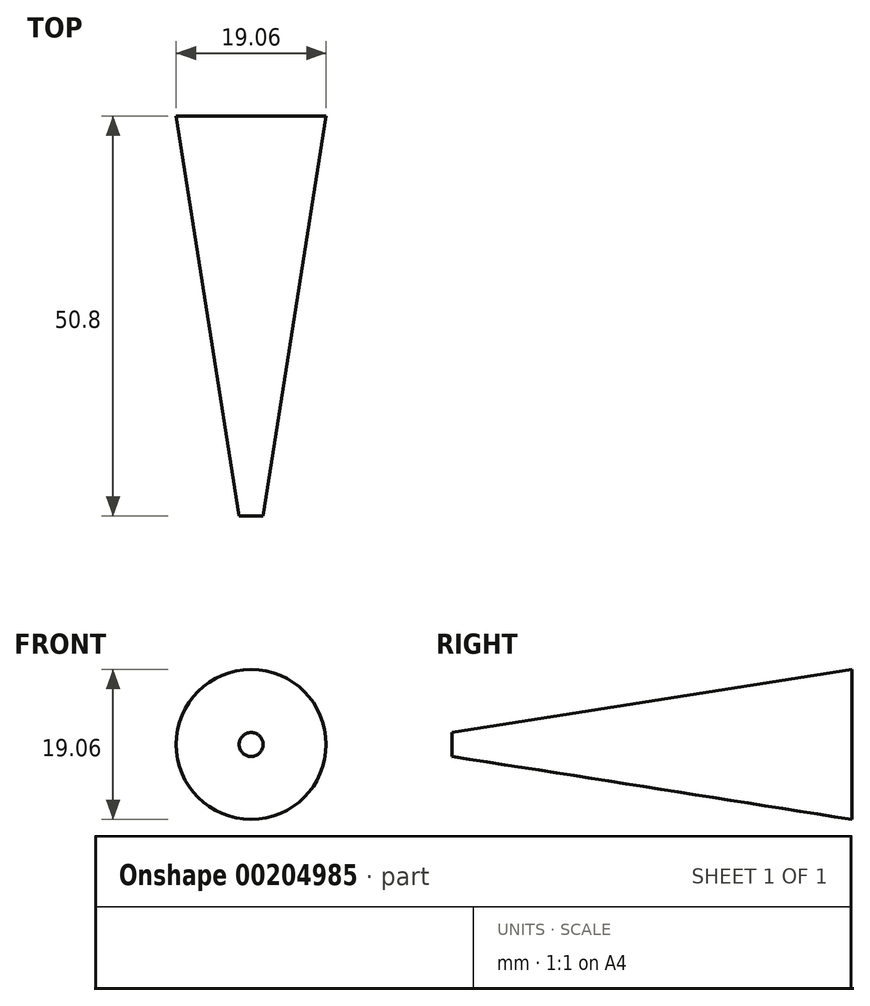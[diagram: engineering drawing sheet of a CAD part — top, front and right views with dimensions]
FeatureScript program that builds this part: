
annotation { "Feature Type Name" : "Feature", "Feature Type Description" : "" }
export const myFeature = defineFeature(function(context is Context, id is Id, definition is map)
    precondition{}
    {
        {
            var Q0;
            Q0=qCreatedBy(makeId("Front.planeOp"),FACE);
            var sketch = newSketch(context, id + "F0", { "sketchPlane" : qUnion([Q0])});
            skCircle(sketch, "E0", {"center": v(0, 0) * mm, "radius": 9.53 * mm});
            skSolve(sketch);
        }
        {
            var Q0;
            Q0=qCreatedBy(makeId("Front.planeOp"),FACE);
            cPlane(context, id + "F1", {"entities" : qUnion([Q0]), "cplaneType" : CPlaneType.OFFSET, "offset" : 50.8 * mm, "width" : 152.4 * mm, "height" : 152.4 * mm});
        }
        {
            var Q0;
            Q0=qCreatedBy(id+"F1.planeOp",FACE);
            var sketch = newSketch(context, id + "F2", { "sketchPlane" : qUnion([Q0])});
            skCircle(sketch, "E1", {"center": v(0, 0) * mm, "radius": 1.52 * mm});
            skSolve(sketch);
        }
        {
            var Q0;
            Q0=makeQuery(id+"F0.imprint","IMPRINT",FACE,{"disambiguationData":[TD([[makeQuery(id+"F0.imprint","IMPRINT",EDGE,{"derivedFrom":sQuery(id+"F0.wireOp",EDGE,"E0")}),1.0]])]});
            var Q1;
            Q1 = qSketchRegion(id + "F2", true);
            loft(context, id + "F3", {"sheetProfilesArray" : [{ "sheetProfileEntities" : qUnion([Q0]) }, { "sheetProfileEntities" : qUnion([Q1]) }]});
        }
    });
